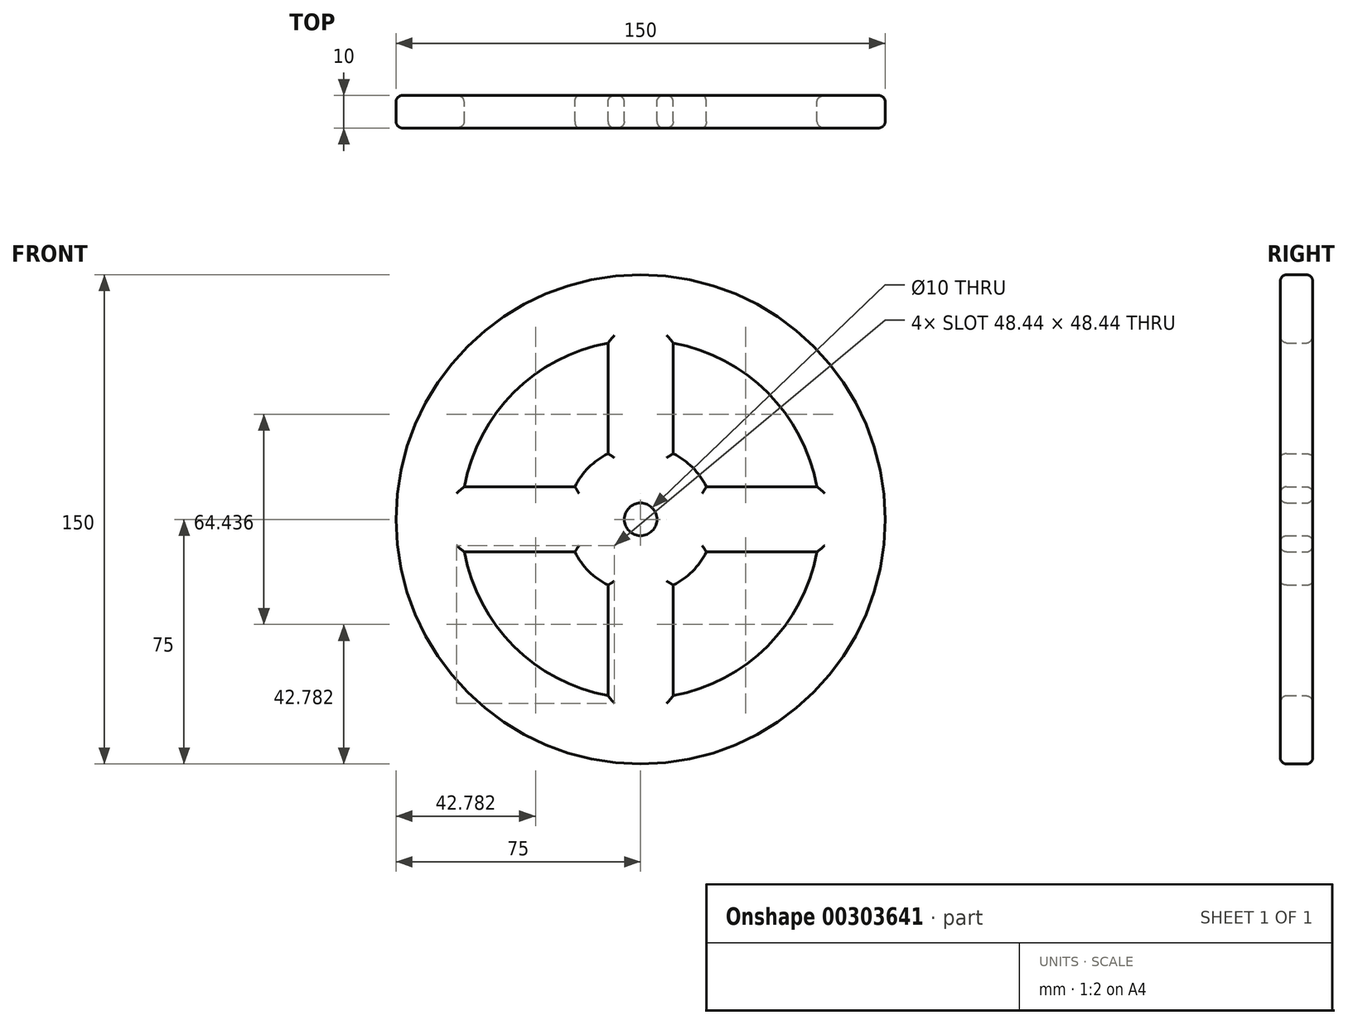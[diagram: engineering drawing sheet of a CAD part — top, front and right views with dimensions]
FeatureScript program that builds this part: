
annotation { "Feature Type Name" : "Feature", "Feature Type Description" : "" }
export const myFeature = defineFeature(function(context is Context, id is Id, definition is map)
    precondition{}
    {
        {
            var Q0;
            Q0=qCreatedBy(makeId("Front.planeOp"),FACE);
            var sketch = newSketch(context, id + "F0", { "sketchPlane" : qUnion([Q0])});
            skCircle(sketch, "E0", {"center": v(0, 0) * mm, "radius": 75 * mm});
            skArc(sketch, "E1", {"start": v(-10, 54.08) * mm, "mid": v(-38.9, 38.9) * mm, "end": v(-54.08, 10) * mm});
            skArc(sketch, "E2", {"start": v(-10, 20.16) * mm, "mid": v(-15.9, 15.9) * mm, "end": v(-20.16, 10) * mm});
            skCircle(sketch, "E3", {"center": v(0, 0) * mm, "radius": 5 * mm});
            skLineSegment(sketch, "E4", {"start": v(0, 0) * mm, "end": v(0, 55) * mm});
            skLineSegment(sketch, "E5", {"start": v(0, 0) * mm, "end": v(55, 0) * mm});
            skLineSegment(sketch, "E6", {"start": v(0, 0) * mm, "end": v(0, -55) * mm});
            skLineSegment(sketch, "E7", {"start": v(0, 0) * mm, "end": v(-55, 0) * mm});
            skLineSegment(sketch, "E8.0", {"start": v(10, 20.16) * mm, "end": v(10, 54.08) * mm});
            skLineSegment(sketch, "E9.0", {"start": v(20.16, -10) * mm, "end": v(54.08, -10) * mm});
            skLineSegment(sketch, "E10.0", {"start": v(-10, -20.16) * mm, "end": v(-10, -54.08) * mm});
            skLineSegment(sketch, "E11.0", {"start": v(10, -20.16) * mm, "end": v(10, -54.08) * mm});
            skLineSegment(sketch, "E12.0", {"start": v(-20.16, -10) * mm, "end": v(-54.08, -10) * mm});
            skArc(sketch, "E13.trimOffspring", {"start": v(54.08, 10) * mm, "mid": v(38.9, 38.9) * mm, "end": v(10, 54.08) * mm});
            skArc(sketch, "E14.trimOffspring", {"start": v(10, -54.08) * mm, "mid": v(38.9, -38.9) * mm, "end": v(54.08, -10) * mm});
            skArc(sketch, "E15.trimOffspring", {"start": v(-54.08, -10) * mm, "mid": v(-38.9, -38.9) * mm, "end": v(-10, -54.08) * mm});
            skLineSegment(sketch, "E16.trimOffspring", {"start": v(-20.16, 10) * mm, "end": v(-54.08, 10) * mm});
            skLineSegment(sketch, "E17.trimOffspring", {"start": v(-10, 20.16) * mm, "end": v(-10, 54.08) * mm});
            skArc(sketch, "E18.trimOffspring", {"start": v(20.16, 10) * mm, "mid": v(15.9, 15.9) * mm, "end": v(10, 20.16) * mm});
            skLineSegment(sketch, "E19.trimOffspring", {"start": v(20.16, 10) * mm, "end": v(54.08, 10) * mm});
            skArc(sketch, "E20.trimOffspring", {"start": v(-20.16, -10) * mm, "mid": v(-15.9, -15.9) * mm, "end": v(-10, -20.16) * mm});
            skArc(sketch, "E21.trimOffspring", {"start": v(10, -20.16) * mm, "mid": v(15.9, -15.9) * mm, "end": v(20.16, -10) * mm});
            skSolve(sketch);
        }
        {
            var Q0;
            Q0 = qSketchRegion(id + "F0", true);
            extrude(context, id + "F1", {"entities" : qUnion([Q0]), "endBound" : BoundingType.SYMMETRIC, "depth" : 10 * mm});
        }
        {
            var Q0;
            Q0=makeQuery(id+"F1.opExtrude","CAP_EDGE",EDGE,{"disambiguationData":[OSD([sQuery(id+"F0.wireOp",EDGE,"E0")])],"isStart":false});
            var Q1;
            Q1=makeQuery(id+"F1.opExtrude","CAP_EDGE",EDGE,{"disambiguationData":[OSD([sQuery(id+"F0.wireOp",EDGE,"E1")])],"isStart":false});
            var Q2;
            Q2=makeQuery(id+"F1.opExtrude","CAP_EDGE",EDGE,{"disambiguationData":[OSD([sQuery(id+"F0.wireOp",EDGE,"E17.trimOffspring")])],"isStart":false});
            var Q3;
            Q3=makeQuery(id+"F1.opExtrude","CAP_EDGE",EDGE,{"disambiguationData":[OSD([sQuery(id+"F0.wireOp",EDGE,"E2")])],"isStart":false});
            var Q4;
            Q4=makeQuery(id+"F1.opExtrude","CAP_EDGE",EDGE,{"disambiguationData":[OSD([sQuery(id+"F0.wireOp",EDGE,"E16.trimOffspring")])],"isStart":false});
            var Q5;
            Q5=makeQuery(id+"F1.opExtrude","CAP_EDGE",EDGE,{"disambiguationData":[OSD([sQuery(id+"F0.wireOp",EDGE,"E12.0")])],"isStart":false});
            var Q6;
            Q6=makeQuery(id+"F1.opExtrude","CAP_EDGE",EDGE,{"disambiguationData":[OSD([sQuery(id+"F0.wireOp",EDGE,"E15.trimOffspring")])],"isStart":false});
            var Q7;
            Q7=makeQuery(id+"F1.opExtrude","CAP_EDGE",EDGE,{"disambiguationData":[OSD([sQuery(id+"F0.wireOp",EDGE,"E10.0")])],"isStart":false});
            var Q8;
            Q8=makeQuery(id+"F1.opExtrude","CAP_EDGE",EDGE,{"disambiguationData":[OSD([sQuery(id+"F0.wireOp",EDGE,"E20.trimOffspring")])],"isStart":false});
            var Q9;
            Q9=makeQuery(id+"F1.opExtrude","CAP_EDGE",EDGE,{"disambiguationData":[OSD([sQuery(id+"F0.wireOp",EDGE,"E21.trimOffspring")])],"isStart":false});
            var Q10;
            Q10=makeQuery(id+"F1.opExtrude","CAP_EDGE",EDGE,{"disambiguationData":[OSD([sQuery(id+"F0.wireOp",EDGE,"E9.0")])],"isStart":false});
            var Q11;
            Q11=makeQuery(id+"F1.opExtrude","CAP_EDGE",EDGE,{"disambiguationData":[OSD([sQuery(id+"F0.wireOp",EDGE,"E14.trimOffspring")])],"isStart":false});
            var Q12;
            Q12=makeQuery(id+"F1.opExtrude","CAP_EDGE",EDGE,{"disambiguationData":[OSD([sQuery(id+"F0.wireOp",EDGE,"E11.0")])],"isStart":false});
            var Q13;
            Q13=makeQuery(id+"F1.opExtrude","CAP_EDGE",EDGE,{"disambiguationData":[OSD([sQuery(id+"F0.wireOp",EDGE,"E3")])],"isStart":false});
            var Q14;
            Q14=makeQuery(id+"F1.opExtrude","CAP_EDGE",EDGE,{"disambiguationData":[OSD([sQuery(id+"F0.wireOp",EDGE,"E18.trimOffspring")])],"isStart":false});
            var Q15;
            Q15=makeQuery(id+"F1.opExtrude","CAP_EDGE",EDGE,{"disambiguationData":[OSD([sQuery(id+"F0.wireOp",EDGE,"E8.0")])],"isStart":false});
            var Q16;
            Q16=makeQuery(id+"F1.opExtrude","CAP_EDGE",EDGE,{"disambiguationData":[OSD([sQuery(id+"F0.wireOp",EDGE,"E13.trimOffspring")])],"isStart":false});
            var Q17;
            Q17=makeQuery(id+"F1.opExtrude","CAP_EDGE",EDGE,{"disambiguationData":[OSD([sQuery(id+"F0.wireOp",EDGE,"E19.trimOffspring")])],"isStart":false});
            var Q18;
            Q18=makeQuery(id+"F1.opExtrude","CAP_EDGE",EDGE,{"disambiguationData":[OSD([sQuery(id+"F0.wireOp",EDGE,"E0")])],"isStart":true});
            var Q19;
            Q19=makeQuery(id+"F1.opExtrude","CAP_EDGE",EDGE,{"disambiguationData":[OSD([sQuery(id+"F0.wireOp",EDGE,"E1")])],"isStart":true});
            var Q20;
            Q20=makeQuery(id+"F1.opExtrude","CAP_EDGE",EDGE,{"disambiguationData":[OSD([sQuery(id+"F0.wireOp",EDGE,"E16.trimOffspring")])],"isStart":true});
            var Q21;
            Q21=makeQuery(id+"F1.opExtrude","CAP_EDGE",EDGE,{"disambiguationData":[OSD([sQuery(id+"F0.wireOp",EDGE,"E2")])],"isStart":true});
            var Q22;
            Q22=makeQuery(id+"F1.opExtrude","CAP_EDGE",EDGE,{"disambiguationData":[OSD([sQuery(id+"F0.wireOp",EDGE,"E17.trimOffspring")])],"isStart":true});
            var Q23;
            Q23=makeQuery(id+"F1.opExtrude","CAP_EDGE",EDGE,{"disambiguationData":[OSD([sQuery(id+"F0.wireOp",EDGE,"E8.0")])],"isStart":true});
            var Q24;
            Q24=makeQuery(id+"F1.opExtrude","CAP_EDGE",EDGE,{"disambiguationData":[OSD([sQuery(id+"F0.wireOp",EDGE,"E13.trimOffspring")])],"isStart":true});
            var Q25;
            Q25=makeQuery(id+"F1.opExtrude","CAP_EDGE",EDGE,{"disambiguationData":[OSD([sQuery(id+"F0.wireOp",EDGE,"E18.trimOffspring")])],"isStart":true});
            var Q26;
            Q26=makeQuery(id+"F1.opExtrude","CAP_EDGE",EDGE,{"disambiguationData":[OSD([sQuery(id+"F0.wireOp",EDGE,"E19.trimOffspring")])],"isStart":true});
            var Q27;
            Q27=makeQuery(id+"F1.opExtrude","CAP_EDGE",EDGE,{"disambiguationData":[OSD([sQuery(id+"F0.wireOp",EDGE,"E21.trimOffspring")])],"isStart":true});
            var Q28;
            Q28=makeQuery(id+"F1.opExtrude","CAP_EDGE",EDGE,{"disambiguationData":[OSD([sQuery(id+"F0.wireOp",EDGE,"E11.0")])],"isStart":true});
            var Q29;
            Q29=makeQuery(id+"F1.opExtrude","CAP_EDGE",EDGE,{"disambiguationData":[OSD([sQuery(id+"F0.wireOp",EDGE,"E14.trimOffspring")])],"isStart":true});
            var Q30;
            Q30=makeQuery(id+"F1.opExtrude","CAP_EDGE",EDGE,{"disambiguationData":[OSD([sQuery(id+"F0.wireOp",EDGE,"E9.0")])],"isStart":true});
            var Q31;
            Q31=makeQuery(id+"F1.opExtrude","CAP_FACE",FACE,{"disambiguationData":[OSD([sQuery(id+"F0.wireOp",EDGE,"E0"),sQuery(id+"F0.wireOp",EDGE,"E1"),sQuery(id+"F0.wireOp",EDGE,"E2"),sQuery(id+"F0.wireOp",EDGE,"E3"),sQuery(id+"F0.wireOp",EDGE,"E8.0"),sQuery(id+"F0.wireOp",EDGE,"E9.0"),sQuery(id+"F0.wireOp",EDGE,"E10.0"),sQuery(id+"F0.wireOp",EDGE,"E11.0"),sQuery(id+"F0.wireOp",EDGE,"E12.0"),sQuery(id+"F0.wireOp",EDGE,"E13.trimOffspring"),sQuery(id+"F0.wireOp",EDGE,"E14.trimOffspring"),sQuery(id+"F0.wireOp",EDGE,"E15.trimOffspring"),sQuery(id+"F0.wireOp",EDGE,"E16.trimOffspring"),sQuery(id+"F0.wireOp",EDGE,"E17.trimOffspring"),sQuery(id+"F0.wireOp",EDGE,"E18.trimOffspring"),sQuery(id+"F0.wireOp",EDGE,"E19.trimOffspring"),sQuery(id+"F0.wireOp",EDGE,"E20.trimOffspring"),sQuery(id+"F0.wireOp",EDGE,"E21.trimOffspring")])],"isStart":true});
            fillet(context, id + "F2", {"entities" : qUnion([Q0, Q1, Q2, Q3, Q4, Q5, Q6, Q7, Q8, Q9, Q10, Q11, Q12, Q13, Q14, Q15, Q16, Q17, Q18, Q19, Q20, Q21, Q22, Q23, Q24, Q25, Q26, Q27, Q28, Q29, Q30, Q31]), "radius" : 2 * mm, "tangentPropagation" : true, "allowEdgeOverflow" : false});
        }
    });
